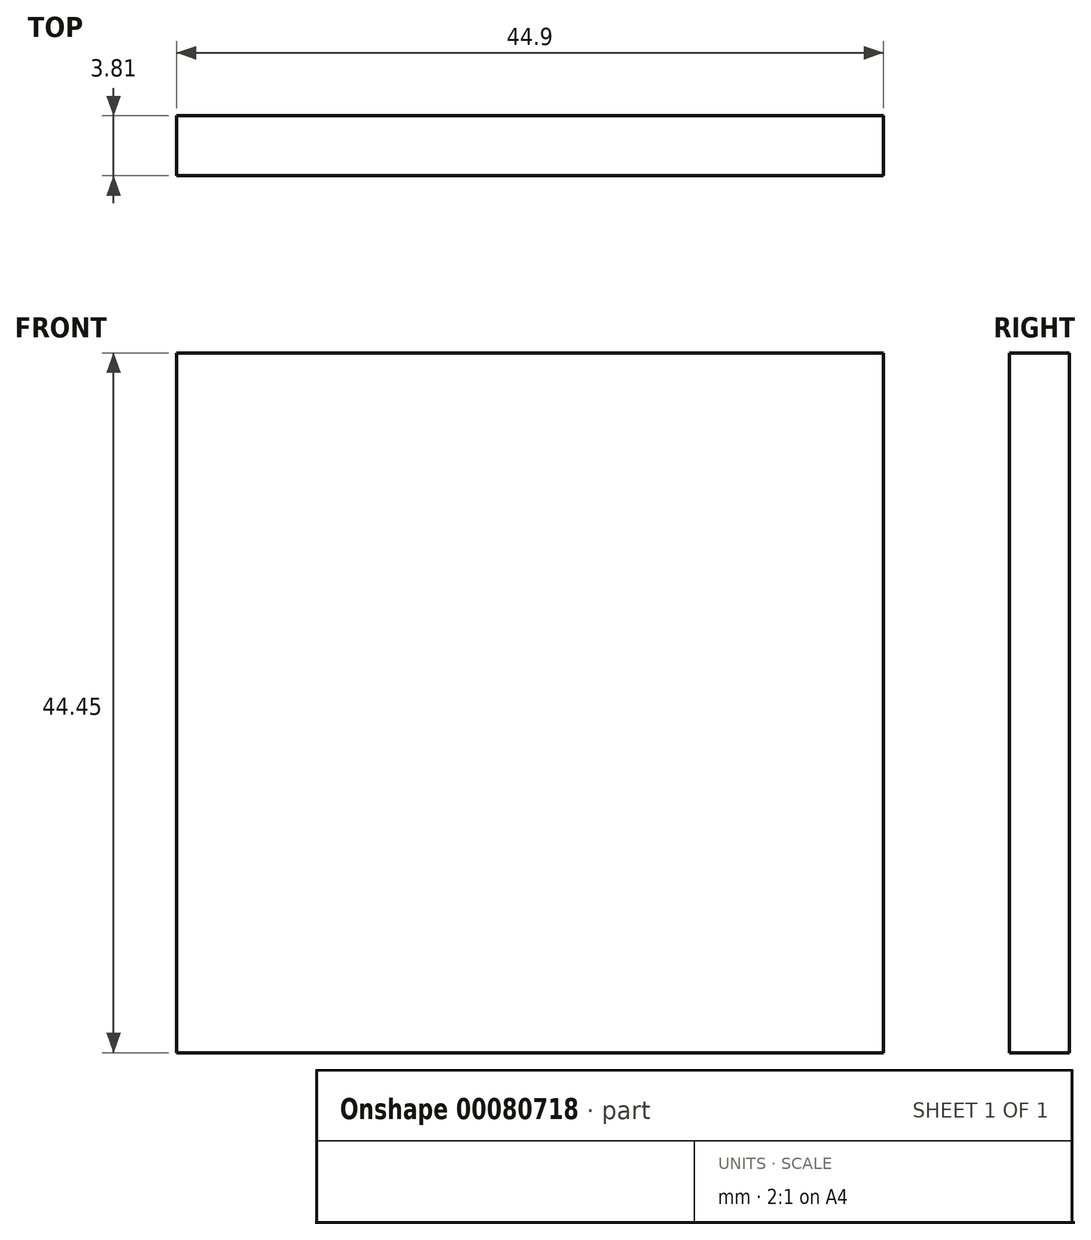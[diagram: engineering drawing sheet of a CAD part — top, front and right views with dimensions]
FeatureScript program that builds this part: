
annotation { "Feature Type Name" : "Feature", "Feature Type Description" : "" }
export const myFeature = defineFeature(function(context is Context, id is Id, definition is map)
    precondition{}
    {
        {
            var Q0;
            Q0=qCreatedBy(makeId("Front.planeOp"),FACE);
            var sketch = newSketch(context, id + "F0", { "sketchPlane" : qUnion([Q0])});
            skLineSegment(sketch, "E0.bottom", {"start": v(-38.5, 33.65) * mm, "end": v(6.41, 33.65) * mm});
            skLineSegment(sketch, "E0.top", {"start": v(-38.5, -10.8) * mm, "end": v(6.41, -10.8) * mm});
            skLineSegment(sketch, "E0.left", {"start": v(-38.5, 33.65) * mm, "end": v(-38.5, -10.8) * mm});
            skLineSegment(sketch, "E0.right", {"start": v(6.41, 33.65) * mm, "end": v(6.41, -10.8) * mm});
            skSolve(sketch);
        }
        {
            var Q0;
            Q0=makeQuery(id+"F0.imprint","IMPRINT",FACE,{"disambiguationData":[TD([[makeQuery(id+"F0.imprint","IMPRINT",EDGE,{"derivedFrom":sQuery(id+"F0.wireOp",EDGE,"E0.bottom")}),-1.0]])]});
            extrude(context, id + "F1", {"entities" : qUnion([Q0]), "depth" : 3.8 * mm});
        }
    });
